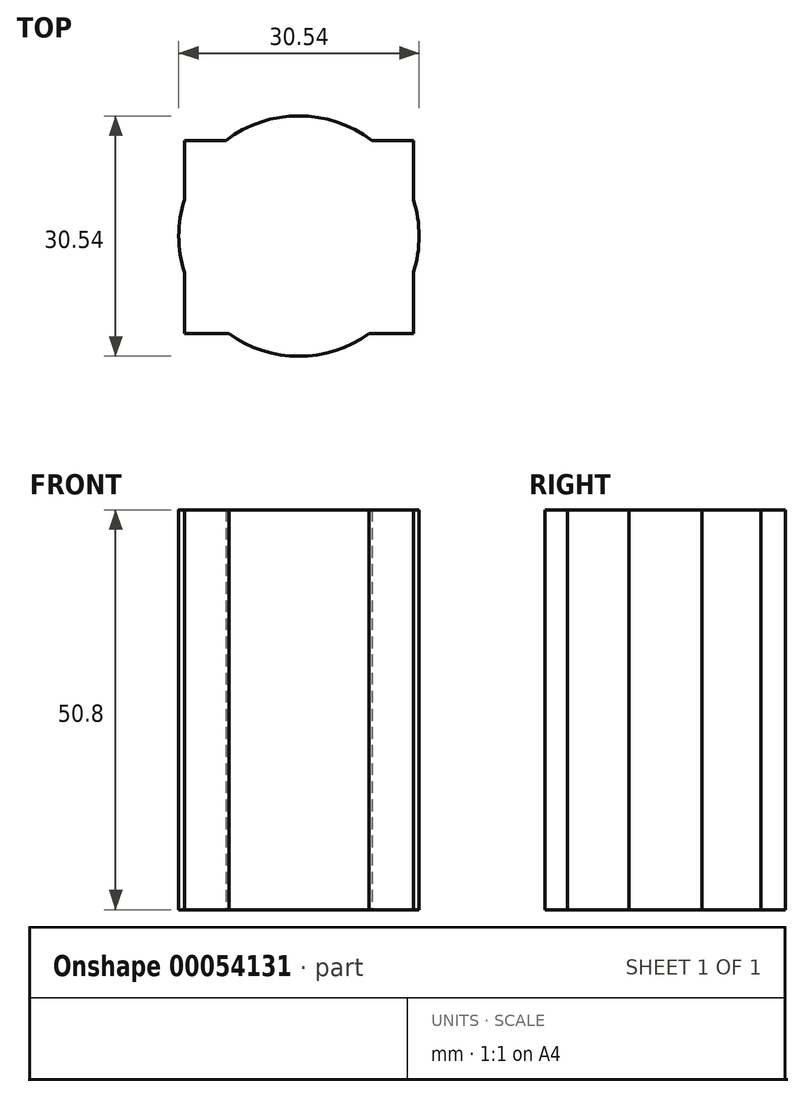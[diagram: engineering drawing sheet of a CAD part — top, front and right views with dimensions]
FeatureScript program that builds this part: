
annotation { "Feature Type Name" : "Feature", "Feature Type Description" : "" }
export const myFeature = defineFeature(function(context is Context, id is Id, definition is map)
    precondition{}
    {
        {
            var Q0;
            Q0=qCreatedBy(makeId("Top.planeOp"),FACE);
            var sketch = newSketch(context, id + "F0", { "sketchPlane" : qUnion([Q0])});
            skCircle(sketch, "E0", {"center": v(0, 0) * mm, "radius": 15.27 * mm});
            skLineSegment(sketch, "E1.bottom", {"start": v(-14.55, 12.12) * mm, "end": v(14.55, 12.12) * mm});
            skLineSegment(sketch, "E1.top", {"start": v(-14.55, -12.4) * mm, "end": v(14.55, -12.4) * mm});
            skLineSegment(sketch, "E1.left", {"start": v(-14.55, 12.12) * mm, "end": v(-14.55, -12.4) * mm});
            skLineSegment(sketch, "E1.right", {"start": v(14.55, 12.12) * mm, "end": v(14.55, -12.4) * mm});
            skPoint(sketch, "E2.orphan", {"position": v(0, 19.67) * mm});
            skLineSegment(sketch, "E3.left", {"start": v(-7.84, 13.1) * mm, "end": v(-7.84, 12.12) * mm});
            skLineSegment(sketch, "E3.right", {"start": v(0, 13.1) * mm, "end": v(0, 12.12) * mm});
            skSolve(sketch);
        }
        {
            var Q0;
            Q0 = qSketchRegion(id + "F0", true);
            extrude(context, id + "F1", {"entities" : qUnion([Q0]), "depth" : 50.8 * mm});
        }
    });
